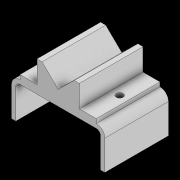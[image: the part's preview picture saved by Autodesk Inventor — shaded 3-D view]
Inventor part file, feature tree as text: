
AUTODESK INVENTOR PART (.ipt)
format: ipt  version: 2021 (Build 250183000, 183)  size: 137,216 bytes
history: native  units: mm
features: extrude x2, sketch x2
ambient origin geometry x8: Origin, YZ Plane, XZ Plane, XY Plane, X Axis, Y Axis, Z Axis, Center Point
bodies: Solid1 (feature_tree)
feature tree (4):
  extrude  "Extrusion1"  Depth=100.0mm
  extrude  "Extrusion4"  Depth=10.0mm
  sketch  "Sketch1"  dims[d0=100.0mm d1=100.0mm]
  sketch  "Sketch4"  dims[d2=80.0mm d4=10.0mm d5=10.0mm d6=150.0mm d7=0.0mm d24=10.0mm d25=50.0mm d26=50.0mm d31=12.0mm d32=12.0mm d33=50.0mm d34=75.0mm d35=15.0mm d36=75.0mm d37=15.0mm d38=20.0mm d39=20.0mm d40=52.0mm d41=52.0mm d42=16.0mm d43=20.0mm d44=20.0mm d45=75.0mm d46=75.0mm d47=50.0mm d48=0.0mm]
